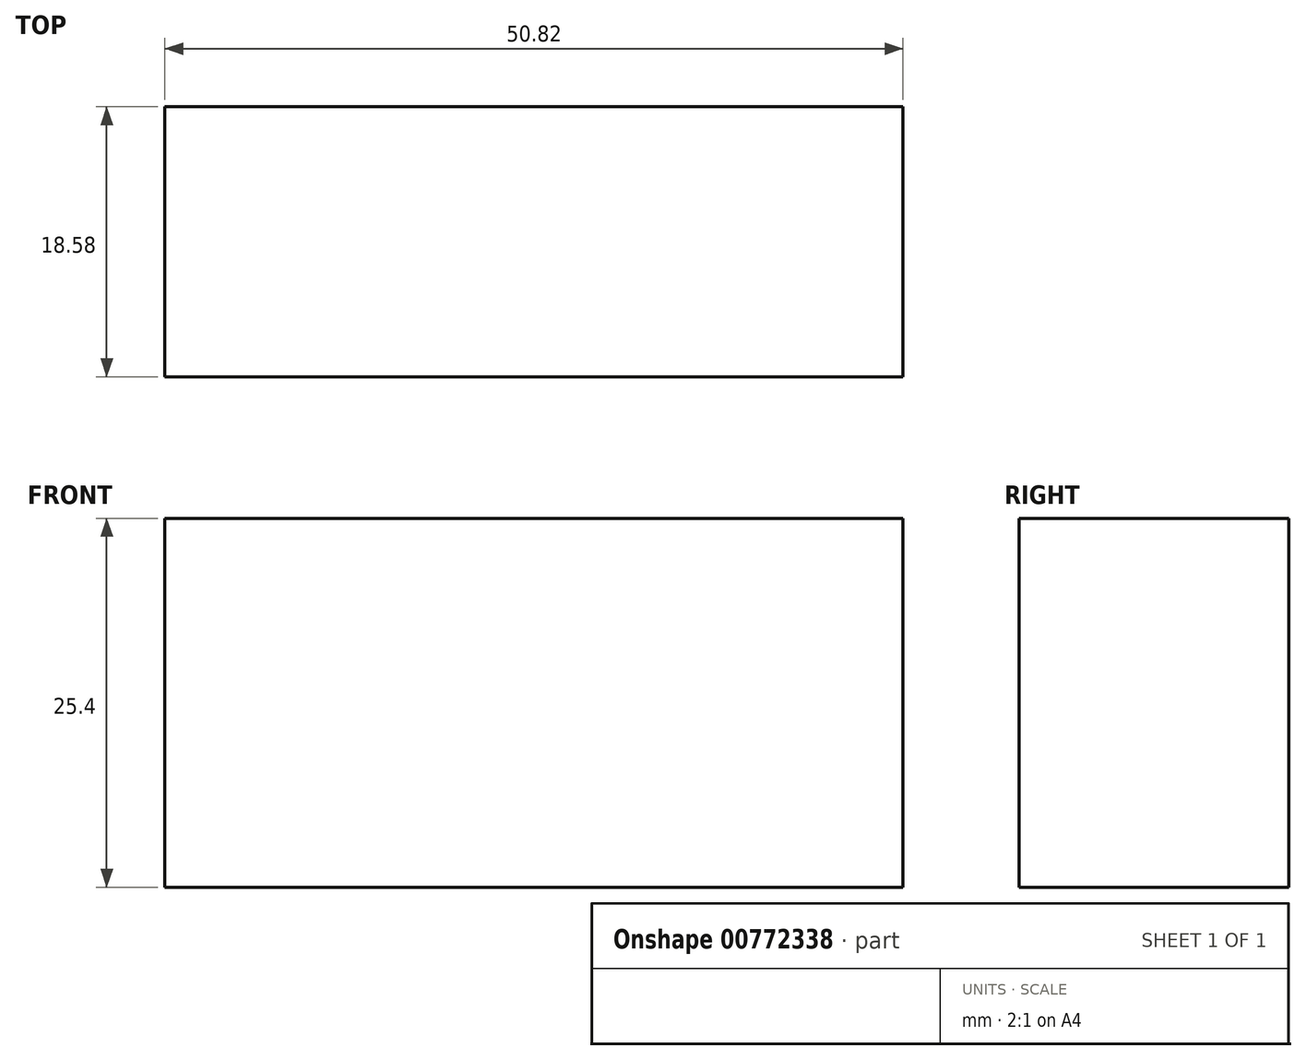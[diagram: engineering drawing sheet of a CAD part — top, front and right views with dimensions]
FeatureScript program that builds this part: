
annotation { "Feature Type Name" : "Feature", "Feature Type Description" : "" }
export const myFeature = defineFeature(function(context is Context, id is Id, definition is map)
    precondition{}
    {
        {
            var Q0;
            Q0=qCreatedBy(makeId("Top.planeOp"),FACE);
            var sketch = newSketch(context, id + "F0", { "sketchPlane" : qUnion([Q0])});
            skLineSegment(sketch, "E0", {"start": v(-36.88, 12.99) * mm, "end": v(13.94, 12.99) * mm});
            skLineSegment(sketch, "E1", {"start": v(-36.88, 12.99) * mm, "end": v(-36.88, -5.6) * mm});
            skLineSegment(sketch, "E2", {"start": v(-36.88, -5.6) * mm, "end": v(13.94, -5.6) * mm});
            skLineSegment(sketch, "E3", {"start": v(13.94, -5.6) * mm, "end": v(13.94, 12.99) * mm});
            skSolve(sketch);
        }
        {
            var Q0;
            Q0 = qSketchRegion(id + "F0", true);
            extrude(context, id + "F1", {"entities" : qUnion([Q0]), "depth" : 25.4 * mm, "offsetDistance" : 25.4 * mm});
        }
    });
